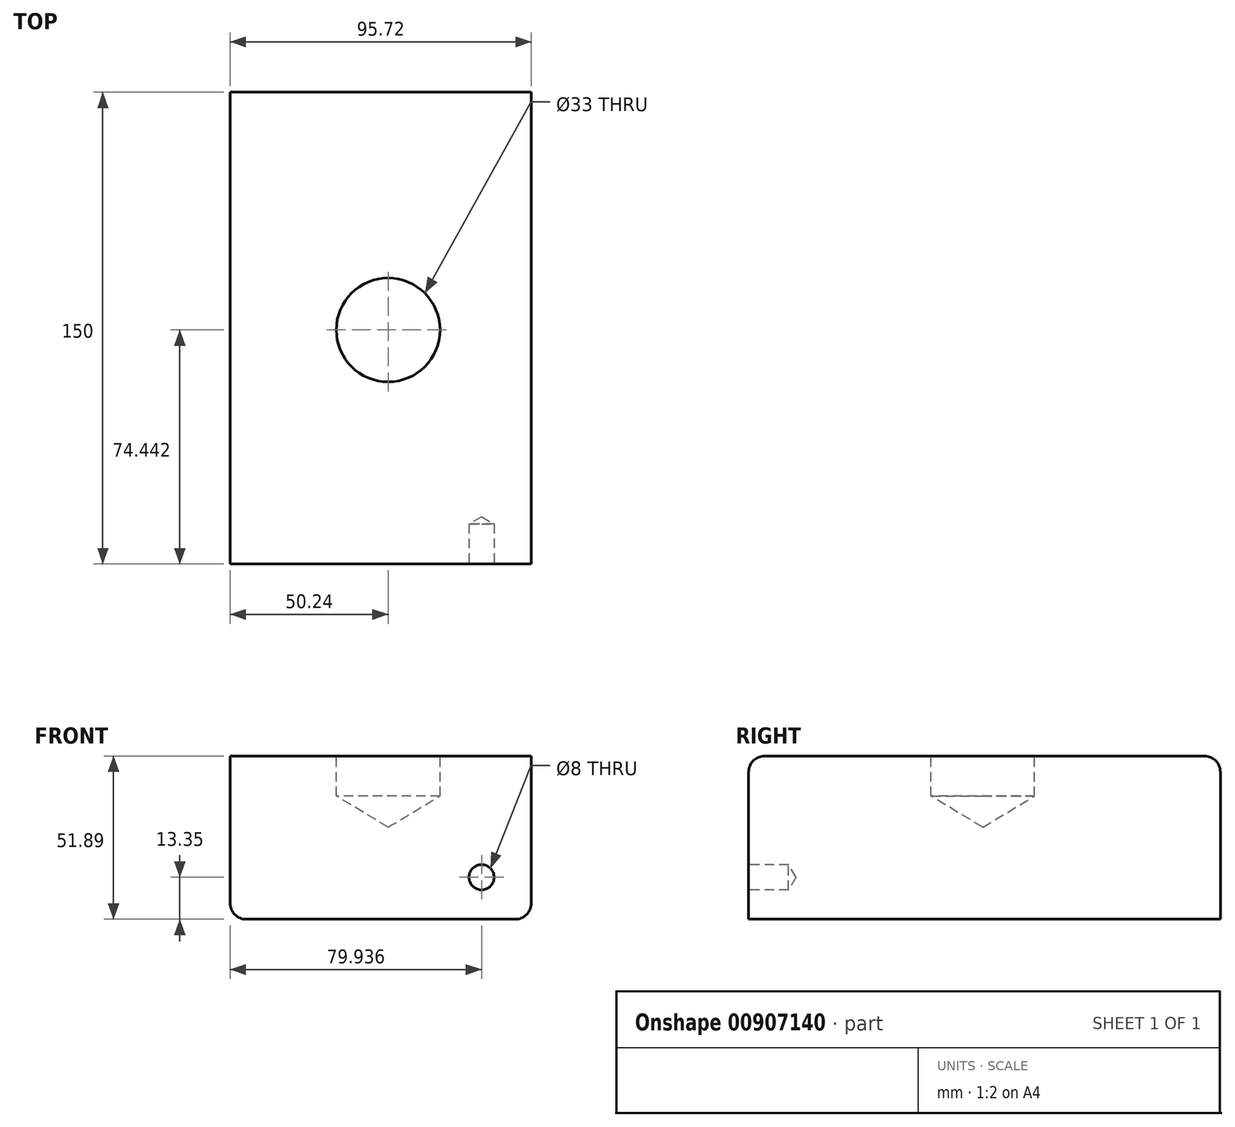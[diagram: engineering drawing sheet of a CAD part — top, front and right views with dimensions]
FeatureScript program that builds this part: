
annotation { "Feature Type Name" : "Feature", "Feature Type Description" : "" }
export const myFeature = defineFeature(function(context is Context, id is Id, definition is map)
    precondition{}
    {
        {
            var Q0;
            Q0=qCreatedBy(makeId("Front.planeOp"),FACE);
            var sketch = newSketch(context, id + "F0", { "sketchPlane" : qUnion([Q0])});
            skLineSegment(sketch, "E0.bottom", {"start": v(-50.24, 38.54) * mm, "end": v(45.48, 38.54) * mm});
            skLineSegment(sketch, "E0.top", {"start": v(-50.24, -13.35) * mm, "end": v(45.48, -13.35) * mm});
            skLineSegment(sketch, "E0.left", {"start": v(-50.24, 38.54) * mm, "end": v(-50.24, -13.35) * mm});
            skLineSegment(sketch, "E0.right", {"start": v(45.48, 38.54) * mm, "end": v(45.48, -13.35) * mm});
            skSolve(sketch);
        }
        {
            var Q0;
            Q0=makeQuery(id+"F0.imprint","IMPRINT",FACE,{"disambiguationData":[TD([[makeQuery(id+"F0.imprint","IMPRINT",EDGE,{"derivedFrom":sQuery(id+"F0.wireOp",EDGE,"E0.bottom")}),-1.0]])]});
            extrude(context, id + "F1", {"entities" : qUnion([Q0]), "depth" : 150 * mm, "offsetDistance" : 25.4 * mm});
        }
        {
            var Q0;
            Q0=makeQuery(id+"F1.opExtrude","CAP_EDGE",EDGE,{"disambiguationData":[OSD([sQuery(id+"F0.wireOp",EDGE,"E0.bottom")])],"isStart":false});
            fillet(context, id + "F2", {"entities" : qUnion([Q0]), "radius" : 5.08 * mm, "tangentPropagation" : true, "allowEdgeOverflow" : false});
        }
        {
            var Q0;
            Q0=makeQuery(id+"F1.opExtrude","CAP_EDGE",EDGE,{"disambiguationData":[OSD([sQuery(id+"F0.wireOp",EDGE,"E0.bottom")])],"isStart":true});
            var Q1;
            Q1=makeQuery(id+"F1.opExtrude","SWEPT_EDGE",EDGE,{"disambiguationData":[OSD([sQuery(id+"F0.wireOp",EDGE,"E0.top"),sQuery(id+"F0.wireOp",EDGE,"E0.right")])]});
            fillet(context, id + "F3", {"entities" : qUnion([Q0, Q1]), "radius" : 5.08 * mm, "tangentPropagation" : true, "allowEdgeOverflow" : false});
        }
        {
            var Q0;
            Q0=makeQuery(id+"F1.opExtrude","SWEPT_EDGE",EDGE,{"disambiguationData":[OSD([sQuery(id+"F0.wireOp",EDGE,"E0.top"),sQuery(id+"F0.wireOp",EDGE,"E0.left")])]});
            fillet(context, id + "F4", {"entities" : qUnion([Q0]), "radius" : 5.08 * mm, "tangentPropagation" : true, "allowEdgeOverflow" : false});
        }
        {
            var Q0;
            Q0=makeQuery(id+"F1.opExtrude","SWEPT_FACE",FACE,{"disambiguationData":[OSD([sQuery(id+"F0.wireOp",EDGE,"E0.bottom")])]});
            var sketch = newSketch(context, id + "F5", { "sketchPlane" : qUnion([Q0])});
            skCircle(sketch, "E1", {"center": v(0, -75.56) * mm, "radius": 7.4 * mm});
            skSolve(sketch);
        }
        {
            var Q0;
            Q0=sQuery(id+"F5.wireOp",VERTEX,"E1.center");
            var Q1;
            Q1=makeQuery(id+"F1.opExtrude","SWEPT_BODY",BODY,{"disambiguationData":[OSD([sQuery(id+"F0.wireOp",EDGE,"E0.bottom"),sQuery(id+"F0.wireOp",EDGE,"E0.top"),sQuery(id+"F0.wireOp",EDGE,"E0.left"),sQuery(id+"F0.wireOp",EDGE,"E0.right")])]});
            hole(context, id + "F6", {"style" : HoleStyle.SIMPLE, "endStyle" : HoleEndStyle.BLIND, "holeDiameter" : 33 * mm, "majorDiameter" : 6.35 * mm, "holeDepth" : 12.7 * mm, "isTappedThrough" : true, "tappedDepth" : 12.7 * mm, "tapClearance" : 3, "locations" : qUnion([Q0]), "scope" : qUnion([Q1])});
        }
        {
            var Q0;
            Q0=makeQuery(id+"F1.opExtrude","CAP_FACE",FACE,{"disambiguationData":[OSD([sQuery(id+"F0.wireOp",EDGE,"E0.bottom"),sQuery(id+"F0.wireOp",EDGE,"E0.top"),sQuery(id+"F0.wireOp",EDGE,"E0.left"),sQuery(id+"F0.wireOp",EDGE,"E0.right")])],"isStart":false});
            var sketch = newSketch(context, id + "F7", { "sketchPlane" : qUnion([Q0])});
            skSolve(sketch);
        }
        {
            var Q0;
            {var subQ0=sQuery(id+"F0.wireOp",EDGE,"E0.right");Q0=makeQuery(id+"F7.imprint","IMPRINT",FACE,{"disambiguationData":[TD([[makeQuery(id+"F7.imprint","IMPRINT",EDGE,{"derivedFrom":makeQuery(id+"F1.opExtrude","CAP_EDGE",EDGE,{"disambiguationData":[OSD([subQ0])],"isStart":false})}),-1.0]])]});}
            var sketch = newSketch(context, id + "F8", { "sketchPlane" : qUnion([Q0])});
            skCircle(sketch, "E2", {"center": v(29.7, 0) * mm, "radius": 3.86 * mm});
            skSolve(sketch);
        }
        {
            var Q0;
            Q0=sQuery(id+"F8.wireOp",VERTEX,"E2.center");
            var Q1;
            Q1=makeQuery(id+"F1.opExtrude","SWEPT_BODY",BODY,{"disambiguationData":[OSD([sQuery(id+"F0.wireOp",EDGE,"E0.bottom"),sQuery(id+"F0.wireOp",EDGE,"E0.top"),sQuery(id+"F0.wireOp",EDGE,"E0.left"),sQuery(id+"F0.wireOp",EDGE,"E0.right")])]});
            hole(context, id + "F9", {"style" : HoleStyle.SIMPLE, "endStyle" : HoleEndStyle.BLIND, "holeDiameter" : 8 * mm, "majorDiameter" : 6.35 * mm, "holeDepth" : 12.7 * mm, "isTappedThrough" : true, "tappedDepth" : 12.7 * mm, "tapClearance" : 3, "locations" : qUnion([Q0]), "scope" : qUnion([Q1])});
        }
    });
